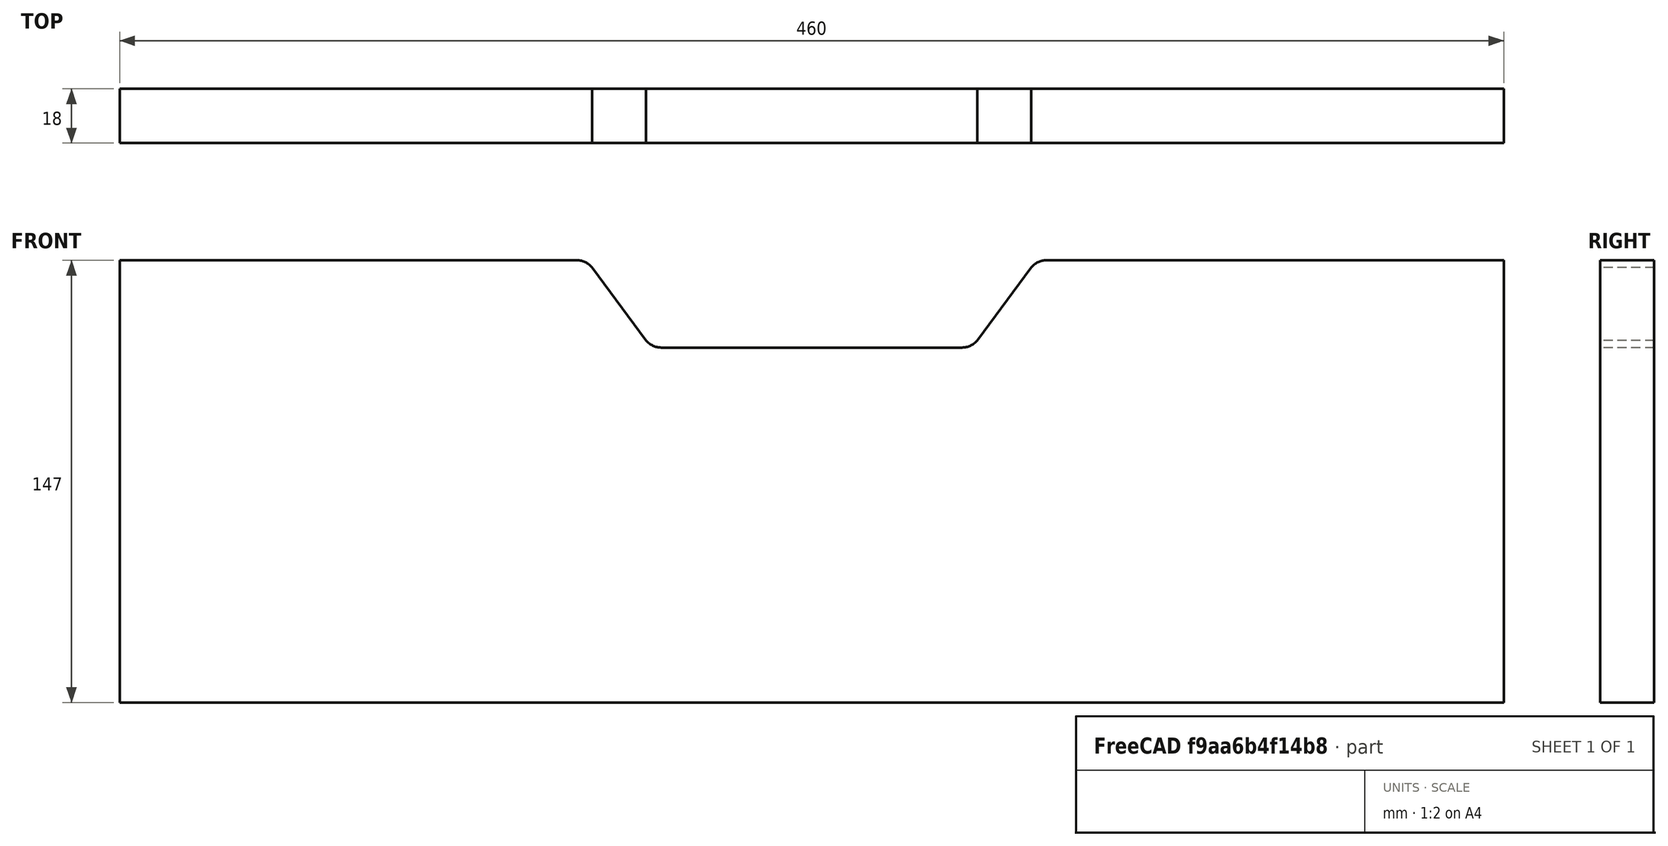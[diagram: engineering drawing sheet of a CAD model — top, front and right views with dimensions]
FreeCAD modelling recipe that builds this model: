
FCSTD DOCUMENT  (FreeCAD 0.18R4 (GitTag))
Label: drawer_false_front
License: All rights reserved
LicenseURL: http://en.wikipedia.org/wiki/All_rights_reserved
objects: Sketcher::SketchObject×1, PartDesign::Pad×1, PartDesign::Body×1
note: 4 computed .brp shape members not serialized (recipe doc carries the construction recipe); baked Part::Feature solids carry a one-line shape summary decoded from their .brp

FEATURE [Sketcher::SketchObject] Sketch
  MapMode = 5
  Placement = pos=(0,0,0) rot=(1,0,0;1.5708rad)
  Support = -> [XZ_Plane]
  sketch-geometry (12):
    g0: LineSegment StartX=0 StartY=0 StartZ=0 EndX=-460 EndY=0 EndZ=0
    g1: LineSegment StartX=-460 StartY=0 StartZ=0 EndX=-460 EndY=147 EndZ=0
    g2: LineSegment StartX=0 StartY=147 StartZ=0 EndX=0 EndY=0 EndZ=0
    g3: LineSegment StartX=-460 StartY=147 StartZ=0 EndX=-308 EndY=147 EndZ=0
    g4: LineSegment StartX=-303 StartY=144.653 StartZ=0 EndX=-285 EndY=120.347 EndZ=0
    g5: LineSegment StartX=-280 StartY=118 StartZ=0 EndX=-180 EndY=118 EndZ=0
    g6: LineSegment StartX=-175 StartY=120.347 StartZ=0 EndX=-157 EndY=144.653 EndZ=0
    g7: LineSegment StartX=-152 StartY=147 StartZ=0 EndX=0 EndY=147 EndZ=0
    g8: ArcOfCircle CenterX=-152 CenterY=140.5 CenterZ=0 NormalX=0 NormalY=0 NormalZ=1 AngleXU=0 Radius=6.5 StartAngle=1.57079 EndAngle=2.44843
    g9: ArcOfCircle CenterX=-180 CenterY=124.5 CenterZ=0 NormalX=0 NormalY=0 NormalZ=1 AngleXU=0 Radius=6.5 StartAngle=4.71239 EndAngle=5.59002
    g10: ArcOfCircle CenterX=-280 CenterY=124.5 CenterZ=0 NormalX=0 NormalY=0 NormalZ=1 AngleXU=0 Radius=6.5 StartAngle=3.83476 EndAngle=4.71239
    g11: ArcOfCircle CenterX=-308 CenterY=140.5 CenterZ=0 NormalX=0 NormalY=0 NormalZ=1 AngleXU=0 Radius=6.5 StartAngle=0.69316 EndAngle=1.5708
  constraints (39):
    c: Coincident(g0,g1)
    c: Coincident(g2,g0)
    c: Horizontal(g0)
    c: Vertical(g1)
    c: Vertical(g2)
    c: Coincident(g0,g-1)
    c: DistanceY(g2,g2) = 147
    c: DistanceX(g0,g0) = 460
    c: Coincident(g7,g2)
    c: Coincident(g9,g5)
    c: Coincident(g9,g6)
    c: Coincident(g6,g8)
    c: Coincident(g8,g7)
    c: Coincident(g10,g5)
    c: Coincident(g10,g4)
    c: Coincident(g3,g11)
    c: Coincident(g11,g4)
    c: Coincident(g3,g1)
    c: DistanceY(g1,g1) = 147
    c: Horizontal(g3)
    c: Horizontal(g5)
    c: Horizontal(g7)
    c: Radius(g11) = 6.5
    c: DistanceY(g11,g3) = 6.5
    c: DistanceX(g3,g3) = 152
    c: DistanceX(g7,g7) = 152
    c: DistanceY(g8,g7) = 6.5
    c: Radius(g8) = 6.5
    c: DistanceY(g5,g7) = 29
    c: DistanceY(g5,g9) = 6.5
    c: Radius(g9) = 6.5
    c: DistanceY(g5,g10) = 6.5
    c: Radius(g10) = 6.5
    c: DistanceX(g5,g5) = 100
    c: DistanceX(g5,g7) = 28
    c: DistanceX(g5,g6) = 5
    c: DistanceX(g6,g7) = 5
    c: DistanceX(g4,g5) = 5
    c: DistanceX(g3,g4) = 5
FEATURE [PartDesign::Pad] Pad
  Length = 18
  Length2 = 100
  Placement = pos=(0,0,0) rot=(1,0,0;1.5708rad)
  Profile = -> Sketch
  Type = 0
FEATURE [PartDesign::Body] Body
  Group = -> [Sketch,Pad]
  Origin = -> Origin
  Tip = -> Pad
